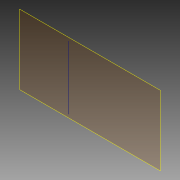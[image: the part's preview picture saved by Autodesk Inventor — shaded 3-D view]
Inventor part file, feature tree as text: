
AUTODESK INVENTOR PART (.ipt)
format: ipt  version: 2013 (Build 170138000, 138)  size: 70,656 bytes
history: native  units: in
note: dims shown in document units (in); Inventor stores cm internally (conversion verified against a paired STEP export)
features: plane x1, extrude x1, sketch x1, reference x1
ambient origin geometry x8: Origin, YZ Plane, XZ Plane, XY Plane, X Axis, Y Axis, Z Axis, Center Point
bodies: Solid1 (feature_tree)
feature tree (4):
  plane  "Work Plane1"
  extrude  "Extrusion1"  Depth=0.1in TaperAngle=0.0deg
  sketch  "Sketch1"  dims[d0=2.0in d2=0.1in d3=0.0in]
  reference  "Reference1"
